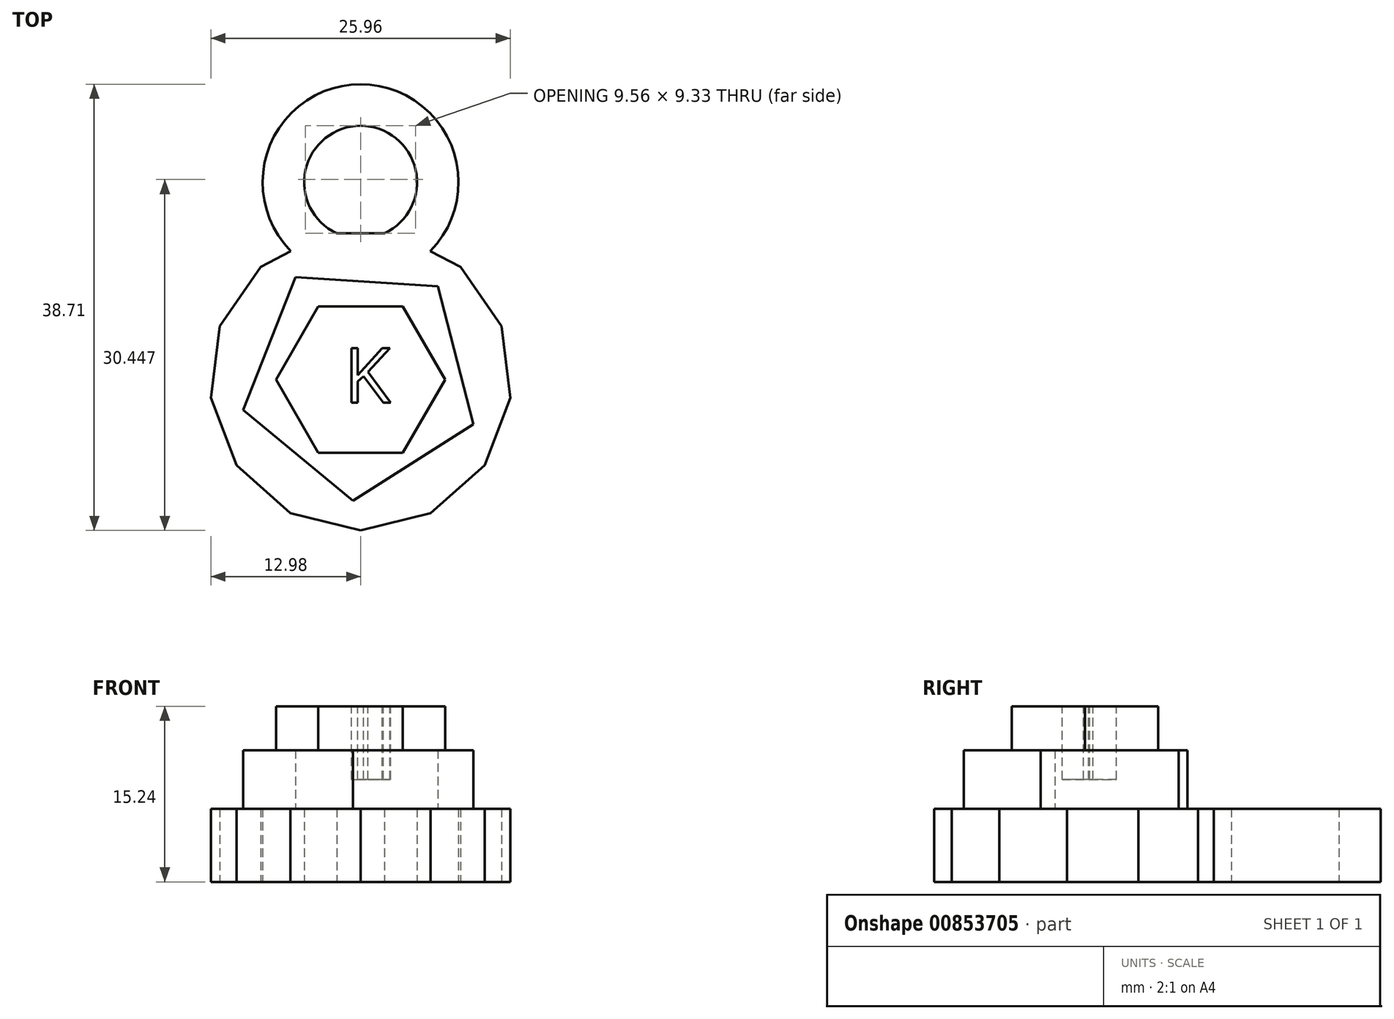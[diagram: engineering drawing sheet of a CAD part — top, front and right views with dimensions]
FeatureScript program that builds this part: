
annotation { "Feature Type Name" : "Feature", "Feature Type Description" : "" }
export const myFeature = defineFeature(function(context is Context, id is Id, definition is map)
    precondition{}
    {
        {
            var Q0;
            Q0=qCreatedBy(makeId("Top.planeOp"),FACE);
            var sketch = newSketch(context, id + "F0", { "sketchPlane" : qUnion([Q0])});
            skCircle(sketch, "E0.cCircle", {"center": v(0, 0) * mm, "radius": 12.7 * mm, "construction": true});
            skLineSegment(sketch, "E0.0", {"start": v(-3.13, 12.7) * mm, "end": v(3.13, 12.7) * mm});
            skLineSegment(sketch, "E0.1", {"start": v(3.13, 12.7) * mm, "end": v(8.67, 9.8) * mm});
            skLineSegment(sketch, "E0.2", {"start": v(8.67, 9.8) * mm, "end": v(12.23, 4.64) * mm});
            skLineSegment(sketch, "E0.3", {"start": v(12.23, 4.64) * mm, "end": v(12.98, -1.58) * mm});
            skLineSegment(sketch, "E0.4", {"start": v(12.98, -1.58) * mm, "end": v(10.76, -7.43) * mm});
            skLineSegment(sketch, "E0.5", {"start": v(10.76, -7.43) * mm, "end": v(6.08, -11.58) * mm});
            skLineSegment(sketch, "E0.6", {"start": v(6.08, -11.58) * mm, "end": v(0, -13.08) * mm});
            skLineSegment(sketch, "E0.7", {"start": v(0, -13.08) * mm, "end": v(-6.08, -11.58) * mm});
            skLineSegment(sketch, "E0.8", {"start": v(-6.08, -11.58) * mm, "end": v(-10.76, -7.43) * mm});
            skLineSegment(sketch, "E0.9", {"start": v(-10.76, -7.43) * mm, "end": v(-12.98, -1.58) * mm});
            skLineSegment(sketch, "E0.10", {"start": v(-12.98, -1.58) * mm, "end": v(-12.23, 4.64) * mm});
            skLineSegment(sketch, "E0.11", {"start": v(-12.23, 4.64) * mm, "end": v(-8.67, 9.8) * mm});
            skLineSegment(sketch, "E0.12", {"start": v(-8.67, 9.8) * mm, "end": v(-3.13, 12.7) * mm});
            skPoint(sketch, "E0.0.midPoint", {"position": v(0, 12.7) * mm});
            skSolve(sketch);
        }
        {
            var Q0;
            Q0=makeQuery(id+"F0.imprint","IMPRINT",FACE,{"disambiguationData":[TD([[makeQuery(id+"F0.imprint","IMPRINT",EDGE,{"derivedFrom":sQuery(id+"F0.wireOp",EDGE,"E0.0")}),-1.0]])]});
            extrude(context, id + "F1", {"entities" : qUnion([Q0]), "depth" : 6.35 * mm, "offsetDistance" : 25.4 * mm});
        }
        {
            var Q0;
            Q0=makeQuery(id+"F1.opExtrude","CAP_FACE",FACE,{"disambiguationData":[OSD([sQuery(id+"F0.wireOp",EDGE,"E0.0"),sQuery(id+"F0.wireOp",EDGE,"E0.1"),sQuery(id+"F0.wireOp",EDGE,"E0.2"),sQuery(id+"F0.wireOp",EDGE,"E0.3"),sQuery(id+"F0.wireOp",EDGE,"E0.4"),sQuery(id+"F0.wireOp",EDGE,"E0.5"),sQuery(id+"F0.wireOp",EDGE,"E0.6"),sQuery(id+"F0.wireOp",EDGE,"E0.7"),sQuery(id+"F0.wireOp",EDGE,"E0.8"),sQuery(id+"F0.wireOp",EDGE,"E0.9"),sQuery(id+"F0.wireOp",EDGE,"E0.10"),sQuery(id+"F0.wireOp",EDGE,"E0.11"),sQuery(id+"F0.wireOp",EDGE,"E0.12")])],"isStart":false});
            var sketch = newSketch(context, id + "F2", { "sketchPlane" : qUnion([Q0])});
            skCircle(sketch, "E1.cCircle", {"center": v(0, 0) * mm, "radius": 8.52 * mm, "construction": true});
            skLineSegment(sketch, "E1.0", {"start": v(-5.65, 8.89) * mm, "end": v(6.7, 8.12) * mm});
            skLineSegment(sketch, "E1.1", {"start": v(6.7, 8.12) * mm, "end": v(9.8, -3.87) * mm});
            skLineSegment(sketch, "E1.2", {"start": v(9.8, -3.87) * mm, "end": v(-0.65, -10.51) * mm});
            skLineSegment(sketch, "E1.3", {"start": v(-0.65, -10.51) * mm, "end": v(-10.2, -2.63) * mm});
            skLineSegment(sketch, "E1.4", {"start": v(-10.2, -2.63) * mm, "end": v(-5.65, 8.89) * mm});
            skPoint(sketch, "E1.0.midPoint", {"position": v(0.53, 8.5) * mm});
            skSolve(sketch);
        }
        {
            var Q0;
            Q0 = qSketchRegion(id + "F2", true);
            extrude(context, id + "F3", {"entities" : qUnion([Q0]), "operationType" : NewBodyOperationType.ADD, "depth" : 5.08 * mm, "offsetDistance" : 25.4 * mm});
        }
        {
            var Q0;
            Q0=makeQuery(id+"F3.opExtrude","CAP_FACE",FACE,{"disambiguationData":[OSD([sQuery(id+"F2.wireOp",EDGE,"E1.0"),sQuery(id+"F2.wireOp",EDGE,"E1.1"),sQuery(id+"F2.wireOp",EDGE,"E1.2"),sQuery(id+"F2.wireOp",EDGE,"E1.3"),sQuery(id+"F2.wireOp",EDGE,"E1.4")])],"isStart":false});
            var sketch = newSketch(context, id + "F4", { "sketchPlane" : qUnion([Q0])});
            skCircle(sketch, "E2.cCircle", {"center": v(0, 0) * mm, "radius": 6.35 * mm, "construction": true});
            skLineSegment(sketch, "E2.0", {"start": v(-3.67, 6.35) * mm, "end": v(3.67, 6.35) * mm});
            skLineSegment(sketch, "E2.1", {"start": v(3.67, 6.35) * mm, "end": v(7.33, 0) * mm});
            skLineSegment(sketch, "E2.2", {"start": v(7.33, 0) * mm, "end": v(3.67, -6.35) * mm});
            skLineSegment(sketch, "E2.3", {"start": v(3.67, -6.35) * mm, "end": v(-3.67, -6.35) * mm});
            skLineSegment(sketch, "E2.4", {"start": v(-3.67, -6.35) * mm, "end": v(-7.33, 0) * mm});
            skLineSegment(sketch, "E2.5", {"start": v(-7.33, 0) * mm, "end": v(-3.67, 6.35) * mm});
            skPoint(sketch, "E2.0.midPoint", {"position": v(0, 6.35) * mm});
            skSolve(sketch);
        }
        {
            var Q0;
            Q0=makeQuery(id+"F4.imprint","IMPRINT",FACE,{"disambiguationData":[TD([[makeQuery(id+"F4.imprint","IMPRINT",EDGE,{"derivedFrom":sQuery(id+"F4.wireOp",EDGE,"E2.0")}),-1.0]])]});
            extrude(context, id + "F5", {"entities" : qUnion([Q0]), "operationType" : NewBodyOperationType.ADD, "depth" : 3.8 * mm, "offsetDistance" : 25.4 * mm});
        }
        {
            var Q0;
            Q0=makeQuery(id+"F5.opExtrude","CAP_FACE",FACE,{"disambiguationData":[OSD([sQuery(id+"F4.wireOp",EDGE,"E2.0"),sQuery(id+"F4.wireOp",EDGE,"E2.1"),sQuery(id+"F4.wireOp",EDGE,"E2.2"),sQuery(id+"F4.wireOp",EDGE,"E2.3"),sQuery(id+"F4.wireOp",EDGE,"E2.4"),sQuery(id+"F4.wireOp",EDGE,"E2.5")])],"isStart":false});
            var sketch = newSketch(context, id + "F6", { "sketchPlane" : qUnion([Q0])});
            skText(sketch, "E3", { "text": "K\n", "fontName": "OpenSans-Regular.ttf"});
            const initialGuessF6  = {"E3": [-0.00144, -0.00198, 1, 0, 0.00475]};
            skSetInitialGuess(sketch, initialGuessF6);
            skSolve(sketch);
        }
        {
            var Q0;
            Q0 = qSketchRegion(id + "F6", true);
            extrude(context, id + "F7", {"entities" : qUnion([Q0]), "operationType" : NewBodyOperationType.REMOVE, "oppositeDirection" : true, "depth" : 6.35 * mm, "offsetDistance" : 25.4 * mm});
        }
        {
            var Q0;
            Q0=qCreatedBy(makeId("Top.planeOp"),FACE);
            var sketch = newSketch(context, id + "F8", { "sketchPlane" : qUnion([Q0])});
            skCircle(sketch, "E4", {"center": v(0, 17.14) * mm, "radius": 8.5 * mm});
            skCircle(sketch, "E5", {"center": v(0, 17.14) * mm, "radius": 4.9 * mm});
            skSolve(sketch);
        }
        {
            var Q0;
            Q0 = qSketchRegion(id + "F8", true);
            var Q1;
            Q1=makeQuery(id+"F1.opExtrude","CAP_FACE",FACE,{"disambiguationData":[OSD([sQuery(id+"F0.wireOp",EDGE,"E0.0"),sQuery(id+"F0.wireOp",EDGE,"E0.1"),sQuery(id+"F0.wireOp",EDGE,"E0.2"),sQuery(id+"F0.wireOp",EDGE,"E0.3"),sQuery(id+"F0.wireOp",EDGE,"E0.4"),sQuery(id+"F0.wireOp",EDGE,"E0.5"),sQuery(id+"F0.wireOp",EDGE,"E0.6"),sQuery(id+"F0.wireOp",EDGE,"E0.7"),sQuery(id+"F0.wireOp",EDGE,"E0.8"),sQuery(id+"F0.wireOp",EDGE,"E0.9"),sQuery(id+"F0.wireOp",EDGE,"E0.10"),sQuery(id+"F0.wireOp",EDGE,"E0.11"),sQuery(id+"F0.wireOp",EDGE,"E0.12")])],"isStart":false});
            extrude(context, id + "F9", {"entities" : qUnion([Q0]), "operationType" : NewBodyOperationType.ADD, "endBound" : BoundingType.UP_TO_SURFACE, "depth" : 25.4 * mm, "endBoundEntityFace" : qUnion([Q1]), "offsetDistance" : 25.4 * mm});
        }
    });
